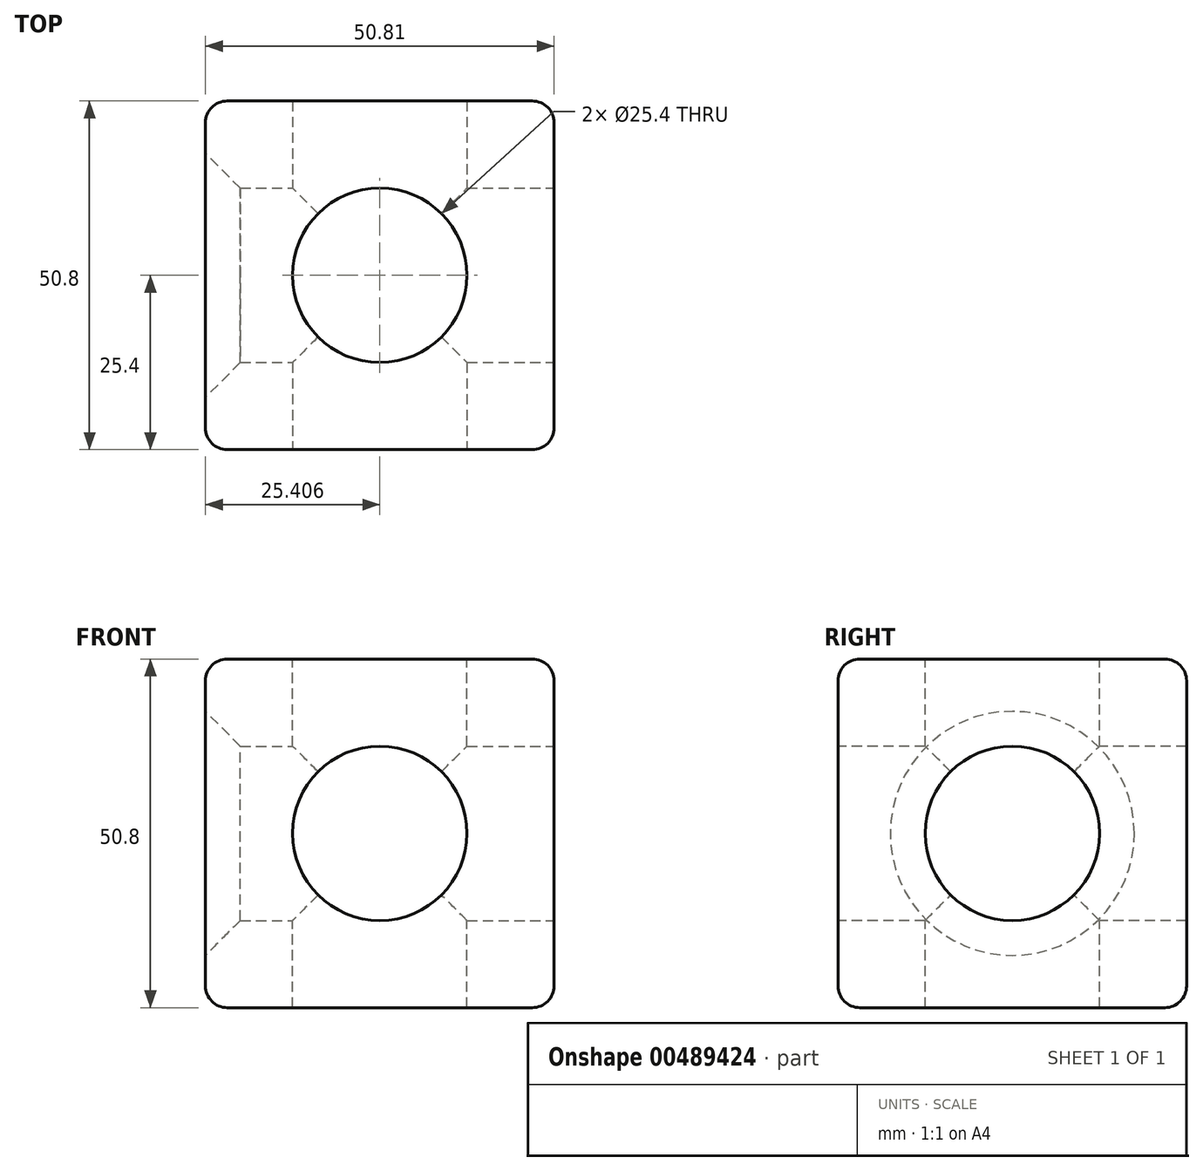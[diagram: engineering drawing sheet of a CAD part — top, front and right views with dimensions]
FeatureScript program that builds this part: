
annotation { "Feature Type Name" : "Feature", "Feature Type Description" : "" }
export const myFeature = defineFeature(function(context is Context, id is Id, definition is map)
    precondition{}
    {
        {
            var Q0;
            Q0=qCreatedBy(makeId("Front.planeOp"),FACE);
            var sketch = newSketch(context, id + "F0", { "sketchPlane" : qUnion([Q0])});
            skLineSegment(sketch, "E0", {"start": v(0, 0) * mm, "end": v(50.81, 0) * mm});
            skLineSegment(sketch, "E1", {"start": v(50.81, 0) * mm, "end": v(50.81, 50.8) * mm});
            skLineSegment(sketch, "E2", {"start": v(50.81, 50.8) * mm, "end": v(0, 50.8) * mm});
            skLineSegment(sketch, "E3", {"start": v(0, 50.8) * mm, "end": v(0, 0) * mm});
            skSolve(sketch);
        }
        {
            var Q0;
            Q0=makeQuery(id+"F0.imprint","IMPRINT",FACE,{"disambiguationData":[TD([[makeQuery(id+"F0.imprint","IMPRINT",EDGE,{"derivedFrom":sQuery(id+"F0.wireOp",EDGE,"E0")}),1.0]])]});
            extrude(context, id + "F1", {"entities" : qUnion([Q0]), "depth" : 50.8 * mm});
        }
        {
            var Q0;
            Q0=makeQuery(id+"F1.opExtrude","CAP_FACE",FACE,{"disambiguationData":[OSD([sQuery(id+"F0.wireOp",EDGE,"E0"),sQuery(id+"F0.wireOp",EDGE,"E1"),sQuery(id+"F0.wireOp",EDGE,"E2"),sQuery(id+"F0.wireOp",EDGE,"E3")])],"isStart":false});
            var sketch = newSketch(context, id + "F2", { "sketchPlane" : qUnion([Q0])});
            skCircle(sketch, "E4", {"center": v(25.4, 25.4) * mm, "radius": 12.7 * mm});
            skPoint(sketch, "E4.centerSnap0", {"position": v(50.81, 25.4) * mm});
            skPoint(sketch, "E4.centerSnap1", {"position": v(25.4, 50.8) * mm});
            skSolve(sketch);
        }
        {
            var Q0;
            Q0=makeQuery(id+"F2.imprint","IMPRINT",FACE,{"disambiguationData":[TD([[makeQuery(id+"F2.imprint","IMPRINT",EDGE,{"derivedFrom":sQuery(id+"F2.wireOp",EDGE,"E4")}),1.0]])]});
            extrude(context, id + "F3", {"entities" : qUnion([Q0]), "operationType" : NewBodyOperationType.REMOVE, "oppositeDirection" : true, "depth" : 50.8 * mm});
        }
        {
            var Q0;
            Q0=makeQuery(id+"F1.opExtrude","SWEPT_FACE",FACE,{"disambiguationData":[OSD([sQuery(id+"F0.wireOp",EDGE,"E1")])]});
            var sketch = newSketch(context, id + "F4", { "sketchPlane" : qUnion([Q0])});
            skCircle(sketch, "E5", {"center": v(-25.4, 25.4) * mm, "radius": 12.7 * mm});
            skPoint(sketch, "E5.centerSnap0", {"position": v(0, 25.4) * mm});
            skPoint(sketch, "E5.centerSnap1", {"position": v(-25.4, 50.8) * mm});
            skSolve(sketch);
        }
        {
            var Q0;
            Q0=makeQuery(id+"F4.imprint","IMPRINT",FACE,{"disambiguationData":[TD([[makeQuery(id+"F4.imprint","IMPRINT",EDGE,{"derivedFrom":sQuery(id+"F4.wireOp",EDGE,"E5")}),1.0]])]});
            extrude(context, id + "F5", {"entities" : qUnion([Q0]), "operationType" : NewBodyOperationType.REMOVE, "oppositeDirection" : true, "depth" : 50.8 * mm});
        }
        {
            var Q0;
            Q0=makeQuery(id+"F5.boolean.opBoolean","COPY",FACE,{"derivedFrom":makeQuery(id+"F5.opExtrude","CAP_FACE",FACE,{"disambiguationData":[OSD([sQuery(id+"F4.wireOp",EDGE,"E5")])],"isStart":false})});
            extrude(context, id + "F6", {"entities" : qUnion([Q0]), "operationType" : NewBodyOperationType.REMOVE, "oppositeDirection" : true, "depth" : 50.8 * mm});
        }
        {
            var Q0;
            Q0=makeQuery(id+"F1.opExtrude","SWEPT_FACE",FACE,{"disambiguationData":[OSD([sQuery(id+"F0.wireOp",EDGE,"E2")])]});
            var sketch = newSketch(context, id + "F7", { "sketchPlane" : qUnion([Q0])});
            skCircle(sketch, "E6", {"center": v(25.4, -25.4) * mm, "radius": 12.7 * mm});
            skPoint(sketch, "E6.centerSnap0", {"position": v(50.81, -25.4) * mm});
            skPoint(sketch, "E6.centerSnap1", {"position": v(25.4, 0) * mm});
            skSolve(sketch);
        }
        {
            var Q0;
            Q0=makeQuery(id+"F7.imprint","IMPRINT",FACE,{"disambiguationData":[TD([[makeQuery(id+"F7.imprint","IMPRINT",EDGE,{"derivedFrom":sQuery(id+"F7.wireOp",EDGE,"E6")}),1.0]])]});
            extrude(context, id + "F8", {"entities" : qUnion([Q0]), "operationType" : NewBodyOperationType.REMOVE, "oppositeDirection" : true, "depth" : 50.8 * mm});
        }
        {
            var Q0;
            Q0=makeQuery(id+"F1.opExtrude","SWEPT_EDGE",EDGE,{"disambiguationData":[OSD([sQuery(id+"F0.wireOp",EDGE,"E1"),sQuery(id+"F0.wireOp",EDGE,"E2")])]});
            var Q1;
            Q1=makeQuery(id+"F1.opExtrude","CAP_EDGE",EDGE,{"disambiguationData":[OSD([sQuery(id+"F0.wireOp",EDGE,"E2")])],"isStart":false});
            var Q2;
            Q2=makeQuery(id+"F1.opExtrude","SWEPT_EDGE",EDGE,{"disambiguationData":[OSD([sQuery(id+"F0.wireOp",EDGE,"E2"),sQuery(id+"F0.wireOp",EDGE,"E3")])]});
            var Q3;
            Q3=makeQuery(id+"F1.opExtrude","CAP_EDGE",EDGE,{"disambiguationData":[OSD([sQuery(id+"F0.wireOp",EDGE,"E2")])],"isStart":true});
            var Q4;
            Q4=makeQuery(id+"F1.opExtrude","CAP_EDGE",EDGE,{"disambiguationData":[OSD([sQuery(id+"F0.wireOp",EDGE,"E1")])],"isStart":false});
            var Q5;
            Q5=makeQuery(id+"F1.opExtrude","CAP_EDGE",EDGE,{"disambiguationData":[OSD([sQuery(id+"F0.wireOp",EDGE,"E1")])],"isStart":true});
            var Q6;
            Q6=makeQuery(id+"F1.opExtrude","SWEPT_EDGE",EDGE,{"disambiguationData":[OSD([sQuery(id+"F0.wireOp",EDGE,"E0"),sQuery(id+"F0.wireOp",EDGE,"E1")])]});
            var Q7;
            Q7=makeQuery(id+"F1.opExtrude","CAP_EDGE",EDGE,{"disambiguationData":[OSD([sQuery(id+"F0.wireOp",EDGE,"E0")])],"isStart":false});
            var Q8;
            Q8=makeQuery(id+"F1.opExtrude","CAP_EDGE",EDGE,{"disambiguationData":[OSD([sQuery(id+"F0.wireOp",EDGE,"E3")])],"isStart":false});
            var Q9;
            Q9=makeQuery(id+"F1.opExtrude","CAP_EDGE",EDGE,{"disambiguationData":[OSD([sQuery(id+"F0.wireOp",EDGE,"E3")])],"isStart":true});
            var Q10;
            Q10=makeQuery(id+"F1.opExtrude","CAP_EDGE",EDGE,{"disambiguationData":[OSD([sQuery(id+"F0.wireOp",EDGE,"E0")])],"isStart":true});
            var Q11;
            Q11=makeQuery(id+"F1.opExtrude","SWEPT_EDGE",EDGE,{"disambiguationData":[OSD([sQuery(id+"F0.wireOp",EDGE,"E0"),sQuery(id+"F0.wireOp",EDGE,"E3")])]});
            fillet(context, id + "F9", {"entities" : qUnion([Q0, Q1, Q2, Q3, Q4, Q5, Q6, Q7, Q8, Q9, Q10, Q11]), "radius" : 3.17 * mm, "tangentPropagation" : true, "allowEdgeOverflow" : false});
        }
        {
            var Q0;
            Q0=makeQuery(id+"F3.boolean.opBoolean","COPY",EDGE,{"derivedFrom":makeQuery(id+"F3.opExtrude","CAP_EDGE",EDGE,{"disambiguationData":[OSD([sQuery(id+"F2.wireOp",EDGE,"E4")])],"isStart":true})});
            var Q1;
            Q1=makeQuery(id+"F8.boolean.opBoolean","COPY",EDGE,{"derivedFrom":makeQuery(id+"F8.opExtrude","CAP_EDGE",EDGE,{"disambiguationData":[OSD([sQuery(id+"F7.wireOp",EDGE,"E6")])],"isStart":false})});
            var Q2;
            Q2=makeQuery(id+"F6.boolean.opBoolean","INTERSECT",EDGE,{"derivedFrom":[makeQuery(id+"F1.opExtrude","SWEPT_FACE",FACE,{"disambiguationData":[OSD([sQuery(id+"F0.wireOp",EDGE,"E3")])]}),makeQuery(id+"F6.opExtrude","SWEPT_FACE",FACE,{"disambiguationData":[OSD([sQuery(id+"F4.wireOp",EDGE,"E5")])]})]});
            var Q3;
            Q3=makeQuery(id+"F3.boolean.opBoolean","COPY",EDGE,{"derivedFrom":makeQuery(id+"F3.opExtrude","CAP_EDGE",EDGE,{"disambiguationData":[OSD([sQuery(id+"F2.wireOp",EDGE,"E4")])],"isStart":false})});
            var Q4;
            Q4=makeQuery(id+"F8.boolean.opBoolean","COPY",EDGE,{"derivedFrom":makeQuery(id+"F8.opExtrude","CAP_EDGE",EDGE,{"disambiguationData":[OSD([sQuery(id+"F7.wireOp",EDGE,"E6")])],"isStart":true})});
            var Q5;
            Q5=makeQuery(id+"F5.boolean.opBoolean","COPY",EDGE,{"derivedFrom":makeQuery(id+"F5.opExtrude","CAP_EDGE",EDGE,{"disambiguationData":[OSD([sQuery(id+"F4.wireOp",EDGE,"E5")])],"isStart":true})});
            chamfer(context, id + "F10", {"entities" : qUnion([Q0, Q1, Q2, Q3, Q4, Q5]), "width" : 5.08 * mm, "tangentPropagation" : true});
        }
    });
